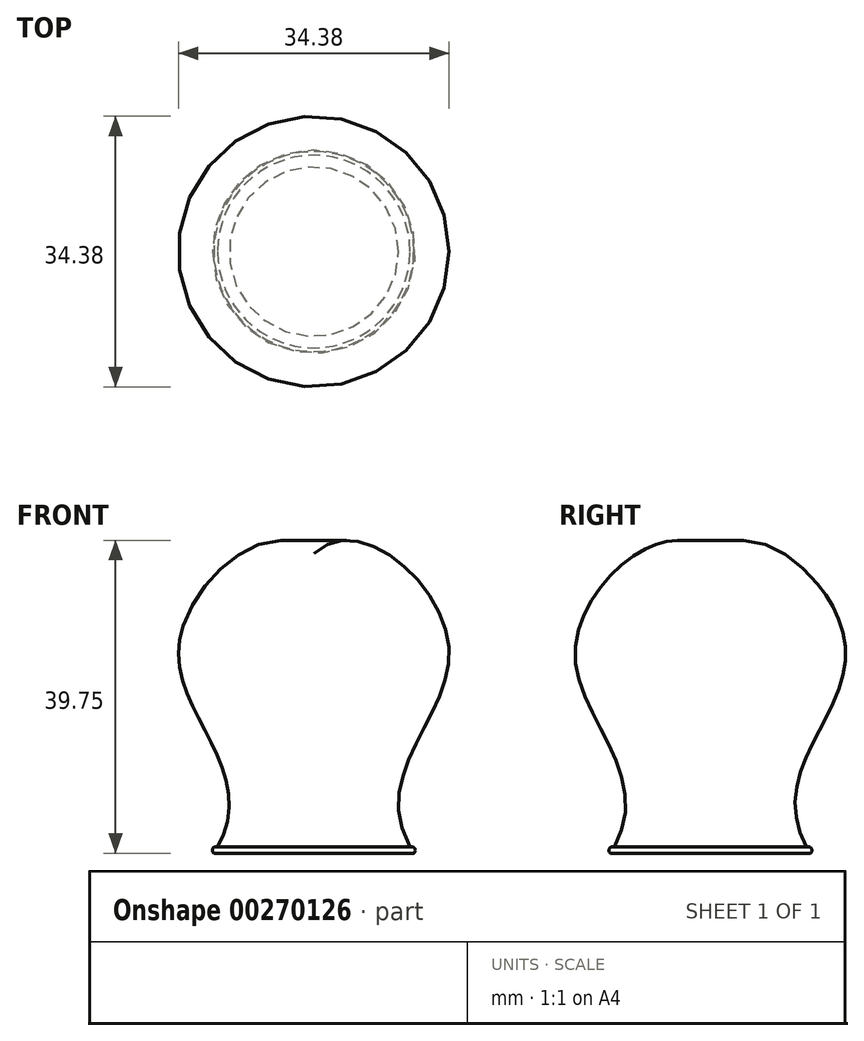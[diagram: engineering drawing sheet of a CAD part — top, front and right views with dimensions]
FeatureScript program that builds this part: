
annotation { "Feature Type Name" : "Feature", "Feature Type Description" : "" }
export const myFeature = defineFeature(function(context is Context, id is Id, definition is map)
    precondition{}
    {
        {
            var Q0;
            Q0=qCreatedBy(makeId("Front.planeOp"),FACE);
            var sketch = newSketch(context, id + "F0", { "sketchPlane" : qUnion([Q0])});
            skLineSegment(sketch, "E0", {"start": v(0, 0) * mm, "end": v(0, 38.1) * mm});
            skLineSegment(sketch, "E1", {"start": v(0, 0) * mm, "end": v(12.7, 0) * mm});
            skFitSpline(sketch, "E2", {"points": [v(0, 38.1) * mm, v(17.15, 26.34) * mm, v(12.7, 0) * mm], "startDerivative": vector(37.67, 35.16) * mm, "endDerivative": vector(36.37, -57.27) * mm});
            skArc(sketch, "E3", {"start": v(12.7, 0) * mm, "mid": v(12.82, 0.61) * mm, "end": v(12.23, 0.8) * mm});
            skSolve(sketch);
        }
        {
            var Q0;
            Q0=makeQuery(id+"F0.imprint","IMPRINT",FACE,{"disambiguationData":[TD([[makeQuery(id+"F0.imprint","IMPRINT",EDGE,{"derivedFrom":sQuery(id+"F0.wireOp",EDGE,"E0")}),-1.0]])]});
            var Q1;
            {var subQ0=sQuery(id+"F0.wireOp",EDGE,"E3");Q1=makeQuery(id+"F0.imprint","IMPRINT",FACE,{"disambiguationData":[TD([[makeQuery(id+"F0.imprint","IMPRINT",EDGE,{"derivedFrom":subQ0}),1.0]])]});}
            var Q2;
            Q2=sQuery(id+"F0.wireOp",EDGE,"E0");
            revolve(context, id + "F1", {"entities" : qUnion([Q0, Q1]), "axis" : qUnion([Q2]), "revolveType" : RevolveType.FULL});
        }
    });
